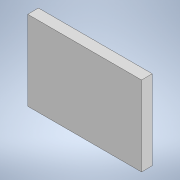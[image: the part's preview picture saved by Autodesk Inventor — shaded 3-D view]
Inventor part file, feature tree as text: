
AUTODESK INVENTOR PART (.ipt)
format: ipt  version: 2020 (Build 240168000, 168)  size: 87,040 bytes
history: native  units: mm
features: extrude x1, sketch x1
ambient origin geometry x8: Origin, YZ Plane, XZ Plane, XY Plane, X Axis, Y Axis, Z Axis, Center Point
bodies: Solide1 (feature_tree)
feature tree (2):
  extrude  "Extrusion1"  Depth=100.0mm
  sketch  "Esquisse1"
